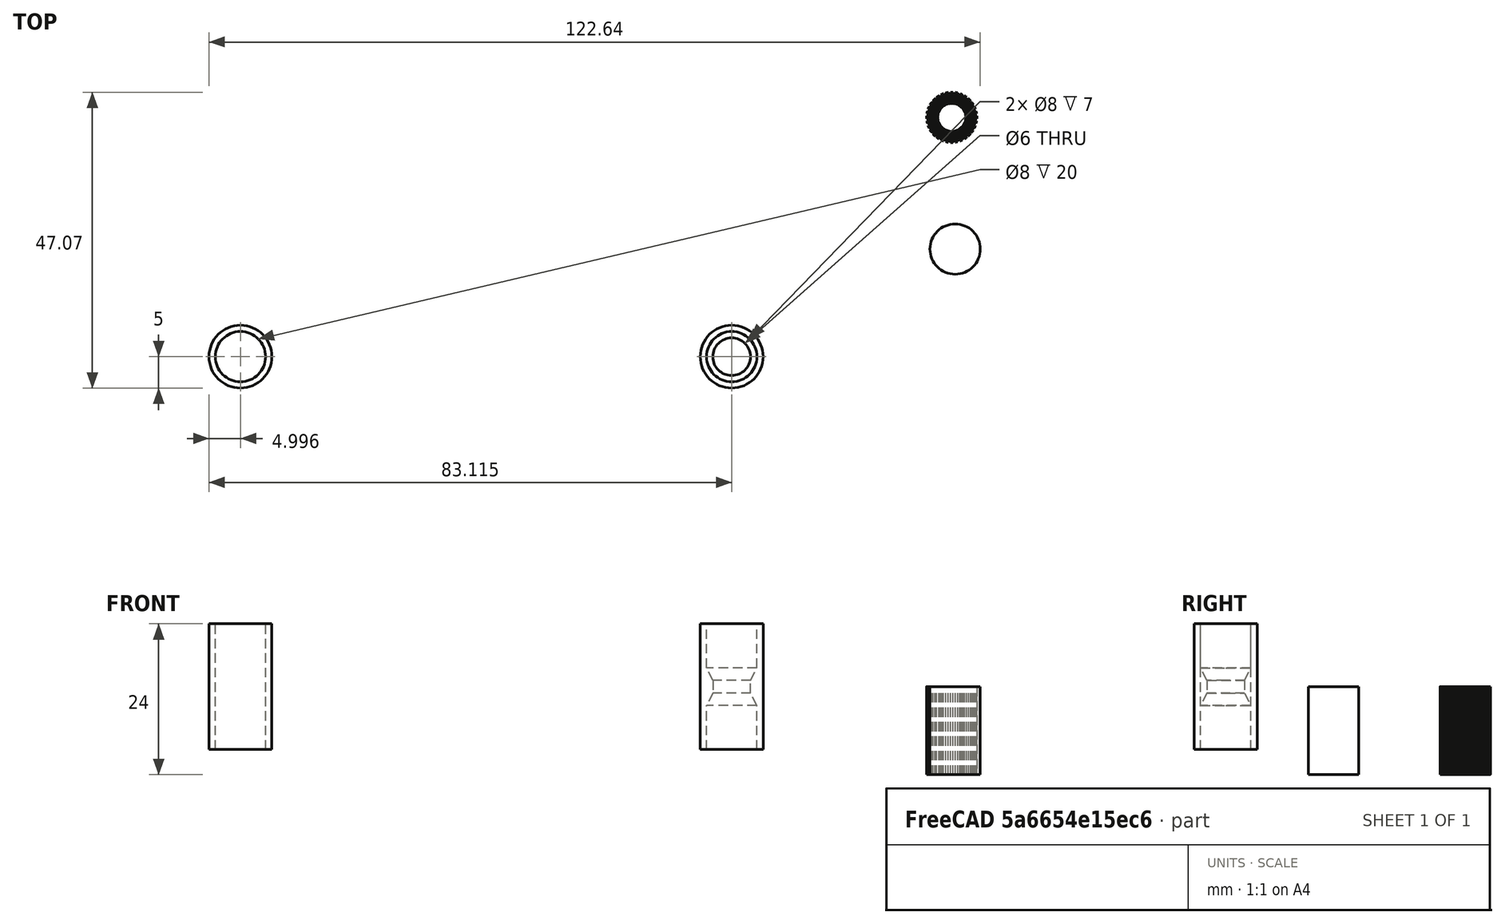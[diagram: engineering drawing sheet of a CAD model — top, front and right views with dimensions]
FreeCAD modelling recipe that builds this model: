
FCSTD DOCUMENT  (FreeCAD 0.20R29177 +426 (Git))
Label: JavaBase
License: All rights reserved
LicenseURL: http://en.wikipedia.org/wiki/All_rights_reserved
objects: Part::Part2DObjectPython×19, Part::Extrusion×19, Part::Cut×5, Part::Cylinder×3, Part::MultiFuse×3, Part::FeaturePython×2, Part::Cone×2, Part::Refine×2, Part::Feature×1
note: 56 computed .brp shape members not serialized (recipe doc carries the construction recipe); baked Part::Feature solids carry a one-line shape summary decoded from their .brp

FEATURE [Part::Cylinder] Cylinder
  Angle = 360
  AttacherType = Attacher::AttachEngine3D
  FirstAngle = 0
  Height = 14
  Placement = pos=(83.0133,17.1126,-4) rot=(0,0,1;0rad)
  Radius = 4
  SecondAngle = 0
FEATURE [Part::Part2DObjectPython] Rectangle  # Draft 2D object (typed FeaturePython)
  Area = 5054.23
  ChamferSize = 0
  Columns = 1
  FilletRadius = 0
  Height = 49.0179
  Length = 103.11
  MakeFace = true
  Placement = pos=(-25.6332,29.8485,0) rot=(1,0,0;3.14159rad)
  Rows = 1
FEATURE [Part::FeaturePython] Tube  # WARN: FeaturePython — macro-defined, semantics opaque (R4)
  AttacherType = Attacher::AttachEngine3D
  Height = 20
  InnerRadius = 4
  OuterRadius = 5
  Placement = pos=(-30.6338,1.9e-15,0) rot=(0,0,1;0rad)
FEATURE [Part::FeaturePython] Tube001  # WARN: FeaturePython — macro-defined, semantics opaque (R4)
  AttacherType = Attacher::AttachEngine3D
  Height = 20
  InnerRadius = 4
  OuterRadius = 5
  Placement = pos=(47.4852,-2.9e-15,0) rot=(0,0,1;0rad)
FEATURE [Part::Cylinder] Cylinder001
  Angle = 360
  AttacherType = Attacher::AttachEngine3D
  FirstAngle = 0
  Height = 4
  Placement = pos=(25.9217,-2e-15,0) rot=(0,0,1;0rad)
  Radius = 4
  SecondAngle = 0
FEATURE [Part::Cylinder] Cylinder002
  Angle = 360
  AttacherType = Attacher::AttachEngine3D
  FirstAngle = 0
  Height = 10
  Placement = pos=(25.9217,-1.8e-15,0) rot=(0,0,1;0rad)
  Radius = 3
  SecondAngle = 0
FEATURE [Part::Cut] Cut
  Base = -> Cylinder001
  Tool = -> Cylinder002
FEATURE [Part::Cone] Cone
  Angle = 360
  AttacherType = Attacher::AttachEngine3D
  Height = 2
  Placement = pos=(25.9217,0,0) rot=(0,0,1;0rad)
  Radius1 = 4
  Radius2 = 3
FEATURE [Part::Feature] Face
  shape: bbox 8 x 8 x 2e-07 mm, 1 faces, 0 solids (baked)
FEATURE [Part::Extrusion] Extrusion
  Base = -> Face
  Dir = (0,0,2)
  DirMode = 0
  FaceMakerClass = Part::FaceMakerBullseye
  LengthFwd = 0
  LengthRev = 0
  Solid = true
  Symmetric = false
FEATURE [Part::MultiFuse] Fusion
  Shapes = -> [Cut,Extrusion]
FEATURE [Part::Cone] Cone001
  Angle = 360
  AttacherType = Attacher::AttachEngine3D
  Height = 2
  Placement = pos=(25.9217,-1.8e-15,4) rot=(0,0,1;0rad)
  Radius1 = 3
  Radius2 = 4
FEATURE [Part::Cut] Cut001
  Base = -> Fusion
  Tool = -> Cone001
FEATURE [Part::Cut] Cut002
  Base = -> Cut001
  Tool = -> Cone
FEATURE [Part::Refine] Cut002001
  Placement = pos=(21.5635,0,7) rot=(0,0,1;0rad)
  Source = -> Cut002
FEATURE [Part::MultiFuse] Fusion001
  Shapes = -> [Tube001,Cut002001]
FEATURE [Part::Part2DObjectPython] Rectangle002  # Draft 2D object (typed FeaturePython)
  Area = 4
  ChamferSize = 0
  Columns = 1
  FilletRadius = 0
  Height = 0.4
  Length = 10
  MakeFace = true
  Placement = pos=(82.268,33.0716,10) rot=(-0.707107,-0.707107,0;3.14159rad)
  Rows = 1
FEATURE [Part::Part2DObjectPython] Rectangle003  # Draft 2D object (typed FeaturePython)
  Area = 4
  ChamferSize = 0
  Columns = 1
  FilletRadius = 0
  Height = 0.4
  Length = 10
  MakeFace = true
  Placement = pos=(78.791,34.6775,10) rot=(-0.92388,-0.382683,0;3.14159rad)
  Rows = 1
FEATURE [Part::Part2DObjectPython] Rectangle004  # Draft 2D object (typed FeaturePython)
  Area = 4
  ChamferSize = 0
  Columns = 1
  FilletRadius = 0
  Height = 0.4
  Length = 10
  MakeFace = true
  Placement = pos=(85.8621,34.3947,10) rot=(-0.382683,-0.92388,0;3.14159rad)
  Rows = 1
FEATURE [Part::Part2DObjectPython] Rectangle005  # Draft 2D object (typed FeaturePython)
  Area = 4
  ChamferSize = 0
  Columns = 1
  FilletRadius = 0
  Height = 0.4
  Length = 10
  MakeFace = true
  Placement = pos=(77.772,36.343,10) rot=(-0.980785,-0.19509,0;3.14159rad)
  Rows = 1
FEATURE [Part::Part2DObjectPython] Rectangle006  # Draft 2D object (typed FeaturePython)
  Area = 4
  ChamferSize = 0
  Columns = 1
  FilletRadius = 0
  Height = 0.4
  Length = 10
  MakeFace = true
  Placement = pos=(80.3698,33.5288,10) rot=(-0.83147,-0.55557,0;3.14159rad)
  Rows = 1
FEATURE [Part::Part2DObjectPython] Rectangle007  # Draft 2D object (typed FeaturePython)
  Area = 4
  ChamferSize = 0
  Columns = 1
  FilletRadius = 0
  Height = 0.4
  Length = 10
  MakeFace = true
  Placement = pos=(84.1966,33.3757,10) rot=(-0.55557,-0.83147,0;3.14159rad)
  Rows = 1
FEATURE [Part::Part2DObjectPython] Rectangle008  # Draft 2D object (typed FeaturePython)
  Area = 4
  ChamferSize = 0
  Columns = 1
  FilletRadius = 0
  Height = 0.4
  Length = 10
  MakeFace = true
  Placement = pos=(77.9251,40.1698,10) rot=(0.980785,-0.19509,0;3.14159rad)
  Rows = 1
FEATURE [Part::Part2DObjectPython] Rectangle009  # Draft 2D object (typed FeaturePython)
  Area = 4
  ChamferSize = 0
  Columns = 1
  FilletRadius = 0
  Height = 0.4
  Length = 10
  MakeFace = true
  Placement = pos=(78.1995,35.4601,10) rot=(-0.95694,-0.290285,0;3.14159rad)
  Rows = 1
FEATURE [Part::Part2DObjectPython] Rectangle010  # Draft 2D object (typed FeaturePython)
  Area = 4
  ChamferSize = 0
  Columns = 1
  FilletRadius = 0
  Height = 0.4
  Length = 10
  MakeFace = true
  Placement = pos=(79.5238,34.0254,10) rot=(-0.881921,-0.471397,0;3.14159rad)
  Rows = 1
FEATURE [Part::Part2DObjectPython] Rectangle011  # Draft 2D object (typed FeaturePython)
  Area = 4
  ChamferSize = 0
  Columns = 1
  FilletRadius = 0
  Height = 0.4
  Length = 10
  MakeFace = true
  Placement = pos=(81.2964,33.2067,10) rot=(-0.77301,-0.634393,0;3.14159rad)
  Rows = 1
FEATURE [Part::Part2DObjectPython] Rectangle012  # Draft 2D object (typed FeaturePython)
  Area = 4
  ChamferSize = 0
  Columns = 1
  FilletRadius = 0
  Height = 0.4
  Length = 10
  MakeFace = true
  Placement = pos=(83.2473,33.1287,10) rot=(-0.634393,-0.77301,0;3.14159rad)
  Rows = 1
FEATURE [Part::Part2DObjectPython] Rectangle013  # Draft 2D object (typed FeaturePython)
  Area = 4
  ChamferSize = 0
  Columns = 1
  FilletRadius = 0
  Height = 0.4
  Length = 10
  MakeFace = true
  Placement = pos=(85.0795,33.8032,10) rot=(-0.471397,-0.881921,0;3.14159rad)
  Rows = 1
FEATURE [Part::Part2DObjectPython] Rectangle014  # Draft 2D object (typed FeaturePython)
  Area = 4
  ChamferSize = 0
  Columns = 1
  FilletRadius = 0
  Height = 0.4
  Length = 10
  MakeFace = true
  Placement = pos=(86.5142,35.1275,10) rot=(-0.290285,-0.95694,0;3.14159rad)
  Rows = 1
FEATURE [Part::Part2DObjectPython] Rectangle015  # Draft 2D object (typed FeaturePython)
  Area = 4
  ChamferSize = 0
  Columns = 1
  FilletRadius = 0
  Height = 0.4
  Length = 10
  MakeFace = true
  Placement = pos=(77.525,37.2923,10) rot=(-0.995185,-0.098017,0;3.14159rad)
  Rows = 1
FEATURE [Part::Part2DObjectPython] Rectangle016  # Draft 2D object (typed FeaturePython)
  Area = 4
  ChamferSize = 0
  Columns = 1
  FilletRadius = 0
  Height = 0.4
  Length = 10
  MakeFace = true
  Placement = pos=(77.6031,39.2432,10) rot=(0.995185,-0.098017,0;3.14159rad)
  Rows = 1
FEATURE [Part::Part2DObjectPython] Rectangle017  # Draft 2D object (typed FeaturePython)
  Area = 4
  ChamferSize = 0
  Columns = 1
  FilletRadius = 0
  Height = 0.4
  Length = 10
  MakeFace = true
  Placement = pos=(77.468,38.2716,10) rot=(1,0,0;3.14159rad)
  Rows = 1
FEATURE [Part::Extrusion] Extrusion001
  Base = -> Rectangle008
  Dir = (0,0,-14)
  DirMode = 0
  FaceMakerClass = Part::FaceMakerBullseye
  LengthFwd = 0
  LengthRev = 0
  Solid = true
  Symmetric = false
FEATURE [Part::Extrusion] Extrusion002
  Base = -> Rectangle014
  Dir = (0,0,-14)
  DirMode = 0
  FaceMakerClass = Part::FaceMakerBullseye
  LengthFwd = 0
  LengthRev = 0
  Solid = true
  Symmetric = false
FEATURE [Part::Extrusion] Extrusion003
  Base = -> Rectangle004
  Dir = (0,0,-14)
  DirMode = 0
  FaceMakerClass = Part::FaceMakerBullseye
  LengthFwd = 0
  LengthRev = 0
  Solid = true
  Symmetric = false
FEATURE [Part::Extrusion] Extrusion004
  Base = -> Rectangle013
  Dir = (0,0,-14)
  DirMode = 0
  FaceMakerClass = Part::FaceMakerBullseye
  LengthFwd = 0
  LengthRev = 0
  Solid = true
  Symmetric = false
FEATURE [Part::Extrusion] Extrusion005
  Base = -> Rectangle007
  Dir = (0,0,-14)
  DirMode = 0
  FaceMakerClass = Part::FaceMakerBullseye
  LengthFwd = 0
  LengthRev = 0
  Solid = true
  Symmetric = false
FEATURE [Part::Extrusion] Extrusion006
  Base = -> Rectangle012
  Dir = (0,0,-14)
  DirMode = 0
  FaceMakerClass = Part::FaceMakerBullseye
  LengthFwd = 0
  LengthRev = 0
  Solid = true
  Symmetric = false
FEATURE [Part::Extrusion] Extrusion007
  Base = -> Rectangle002
  Dir = (0,0,-14)
  DirMode = 0
  FaceMakerClass = Part::FaceMakerBullseye
  LengthFwd = 0
  LengthRev = 0
  Solid = true
  Symmetric = false
FEATURE [Part::Extrusion] Extrusion008
  Base = -> Rectangle011
  Dir = (0,0,-14)
  DirMode = 0
  FaceMakerClass = Part::FaceMakerBullseye
  LengthFwd = 0
  LengthRev = 0
  Solid = true
  Symmetric = false
FEATURE [Part::Extrusion] Extrusion009
  Base = -> Rectangle006
  Dir = (0,0,-14)
  DirMode = 0
  FaceMakerClass = Part::FaceMakerBullseye
  LengthFwd = 0
  LengthRev = 0
  Solid = true
  Symmetric = false
FEATURE [Part::Extrusion] Extrusion010
  Base = -> Rectangle010
  Dir = (0,0,-14)
  DirMode = 0
  FaceMakerClass = Part::FaceMakerBullseye
  LengthFwd = 0
  LengthRev = 0
  Solid = true
  Symmetric = false
FEATURE [Part::Extrusion] Extrusion011
  Base = -> Rectangle003
  Dir = (0,0,-14)
  DirMode = 0
  FaceMakerClass = Part::FaceMakerBullseye
  LengthFwd = 0
  LengthRev = 0
  Solid = true
  Symmetric = false
FEATURE [Part::Extrusion] Extrusion012
  Base = -> Rectangle016
  Dir = (0,0,-14)
  DirMode = 0
  FaceMakerClass = Part::FaceMakerBullseye
  LengthFwd = 0
  LengthRev = 0
  Solid = true
  Symmetric = false
FEATURE [Part::Extrusion] Extrusion013
  Base = -> Rectangle017
  Dir = (0,0,-14)
  DirMode = 0
  FaceMakerClass = Part::FaceMakerBullseye
  LengthFwd = 0
  LengthRev = 0
  Solid = true
  Symmetric = false
FEATURE [Part::Extrusion] Extrusion014
  Base = -> Rectangle015
  Dir = (0,0,-14)
  DirMode = 0
  FaceMakerClass = Part::FaceMakerBullseye
  LengthFwd = 0
  LengthRev = 0
  Solid = true
  Symmetric = false
FEATURE [Part::Extrusion] Extrusion015
  Base = -> Rectangle005
  Dir = (0,0,-14)
  DirMode = 0
  FaceMakerClass = Part::FaceMakerBullseye
  LengthFwd = 0
  LengthRev = 0
  Solid = true
  Symmetric = false
FEATURE [Part::Extrusion] Extrusion016
  Base = -> Rectangle009
  Dir = (0,0,-14)
  DirMode = 0
  FaceMakerClass = Part::FaceMakerBullseye
  LengthFwd = 0
  LengthRev = 0
  Solid = true
  Symmetric = false
FEATURE [Part::MultiFuse] Fusion002
  Shapes = -> [Extrusion006,Extrusion007,Extrusion008,Extrusion009,Extrusion010,Extrusion011,Extrusion016,Extrusion015,Extrusion014,Extrusion013,Extrusion012,Extrusion001,Extrusion002,Extrusion003,Extrusion004,Extrusion005]
FEATURE [Part::Refine] Fusion002001
  Source = -> Fusion002
FEATURE [Part::Part2DObjectPython] Circle  # Draft 2D object (typed FeaturePython)
  Area = 50.2655
  FirstAngle = 0
  LastAngle = 0
  MakeFace = true
  Placement = pos=(82.468,38.0716,10) rot=(0,0,1;0rad)
  Radius = 4
FEATURE [Part::Extrusion] Extrusion017
  Base = -> Circle
  Dir = (0,0,-23.3678)
  DirMode = 0
  FaceMakerClass = Part::FaceMakerBullseye
  LengthFwd = 0
  LengthRev = 0
  Solid = true
  Symmetric = false
FEATURE [Part::Part2DObjectPython] Circle001  # Draft 2D object (typed FeaturePython)
  Area = 433.234
  FirstAngle = 0
  LastAngle = 0
  MakeFace = true
  Placement = pos=(82.468,38.0716,10) rot=(0,0,1;0rad)
  Radius = 11.7432
FEATURE [Part::Extrusion] Extrusion018
  Base = -> Circle001
  Dir = (0,0,-23.3678)
  DirMode = 0
  FaceMakerClass = Part::FaceMakerBullseye
  LengthFwd = 0
  LengthRev = 0
  Solid = true
  Symmetric = false
FEATURE [Part::Cut] Cut002002
  Base = -> Extrusion018
  Tool = -> Extrusion017
FEATURE [Part::Cut] Cut002003
  Base = -> Fusion002001
  Tool = -> Cut002002
